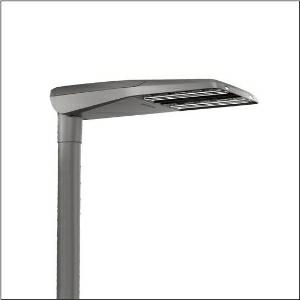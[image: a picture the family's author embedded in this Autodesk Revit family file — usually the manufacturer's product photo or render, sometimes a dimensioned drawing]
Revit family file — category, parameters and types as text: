
# Revit family: streetlight_sl_11_iq_midi___st1_2a_5xc3a51e08me_cf1e
name_source: partatom
category: Lighting Fixtures
units: mm (PartAtom-declared; Revit-internal decimal feet)

## family parameters
Cut with Voids When Loaded = No
Host = Face
Light Source = No
Part Type = Normal
Room Calculation Point = No
Round Connector Dimension = Use Diameter
Shared = No

## types (1)
- --- (1 x LED, 18110 lm, 124.7 W, 3000K)
    Apparent Load = 125 VA
    CIE Flux Codes = 32 70 96 100 100
    Color Rendering = 70
    Color Temperature = 3000K
    Default Elevation = 1800 mm
    Description = Streetlight SL 11 iQ midi, mast luminaire, primary light control with 3 zone facetted reflector, of plastic, silver coated, highly specular, primary optical cover: cover, of PMMA, transparent, light distribution: ST1.2a, light emission: direct distribution, primary light characteristic: asymmetric, installation type: post-top, side-entry, LED, High Power LED, rated luminous flux: 18.110lm, luminous efficacy: 145lm/W, light colour: 730, colour temperature: 3000K, control: optimised constant luminous flux control (CLO 2.0), Desk-Remote (wireless, voltage-free reading and setting of iQ features in the workshop via application-optimized NFC function/RFID function), Light-Fading, Smart-Wire, Night-Set, Lumen-Switch, Temp-Guard, Auto-Match, with cable H07RN-F 5x 1.5mm², mains connection: 220..240V, AC, 50/60Hz, connection cable pre-assembled, cable length: 12,5m, start of lifetime: 125W, end of lifetime: 132W, reduction: 57W, luminaire housing, of diecast aluminium, powder-coated, Siteco® metallic grey (DB 702S), length: 780mm, width: 376mm, height: 118mm, spigot size: 60/76mm (post-top) and 42/60/76mm (side-entry), mast flange for spigot size: 42mm: 5XC10008XM4, 60mm: 5XC10008XM2, 76/60mm: 5XC10108XM1, equipment: Power, protection rating (complete): IP66, insulation class (complete): insulation class II (safety insulation), certification: CE, ENEC, VDE, impact resistance: IK09, permissible operating ambient temperature for outdoor applications: -25..+50°C, standard-compliant lighting for roads and squares, packaging unit: 1 piece

Light Distribution: ST1.2a
    Height = 118 mm
    Lamp = 1 x LED
    Lamp Light Flux = 18110 lm
    Lamp Power = 124.7 W
    Lamp count = 1
    Length = 780 mm
    Luminous efficacy = 145 lm/W
    Manufacturer = Siteco
    ModVariant = No
    Model = 5XC3A51E08ME
    Number of Poles = 1
    OnlyDefault = Yes
    Power Factor = 1
    Product Name = Streetlight SL 11 iQ midi | ST1.2a
    Product group = mast luminaire | pylon top
    ProductGroupID = 6100
    Protection Class = Protection class II
    Protection Degree = IP 66
    RLX_Detail_Level = 1
    RlxData = <blob elided: 70425 chars, md5=f3240837>
    Socket = socket
    Standby Power = 0 W
    System Light Flux = 18110 lm
    System Power = 125 W
    Type Comments = factory setting: luminous flux: 100 % | dim-lin: 254 | 557 mA
    Type Image = l_1005960.jpg
    URL = http://relux.com
    VarID = @adj_118819
    Voltage = 0 V
    Weight = 0.00 kg
    Width = 376 mm

## geometry (parser evidence)
native form markers: Blend x4, Sweep x9
no freeform markers — native parametric forms only
